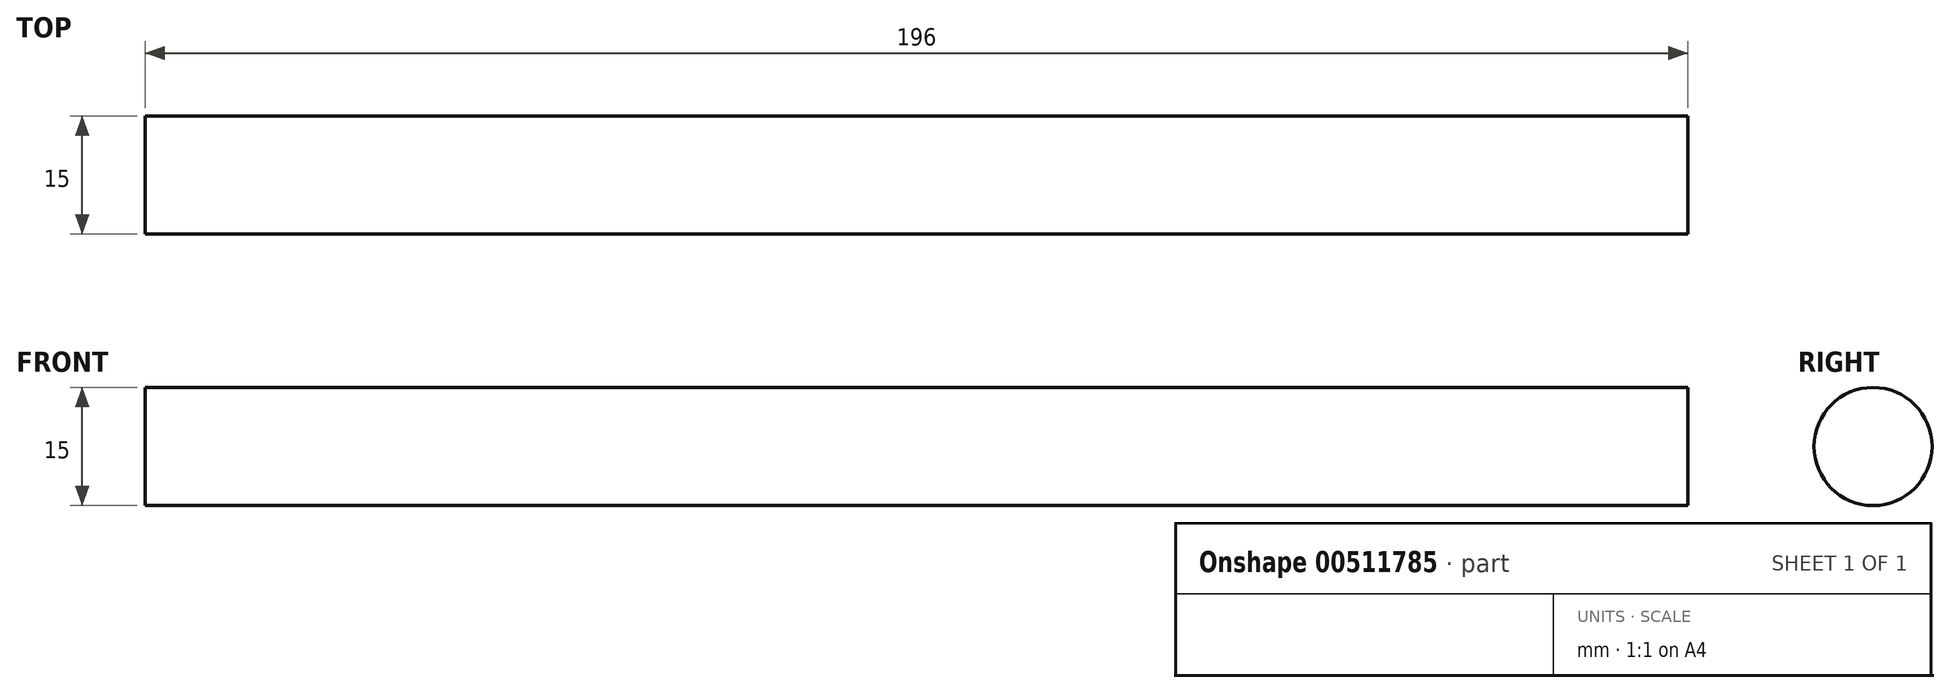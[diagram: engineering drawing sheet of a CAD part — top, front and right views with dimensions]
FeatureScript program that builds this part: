
annotation { "Feature Type Name" : "Feature", "Feature Type Description" : "" }
export const myFeature = defineFeature(function(context is Context, id is Id, definition is map)
    precondition{}
    {
        {
            var Q0;
            Q0=qCreatedBy(makeId("Right.planeOp"),FACE);
            var sketch = newSketch(context, id + "F0", { "sketchPlane" : qUnion([Q0])});
            skCircle(sketch, "E0", {"center": v(0, 0) * mm, "radius": 7.5 * mm});
            skSolve(sketch);
        }
        {
            var Q0;
            Q0 = qSketchRegion(id + "F0", true);
            extrude(context, id + "F1", {"entities" : qUnion([Q0]), "depth" : 196 * mm});
        }
    });
